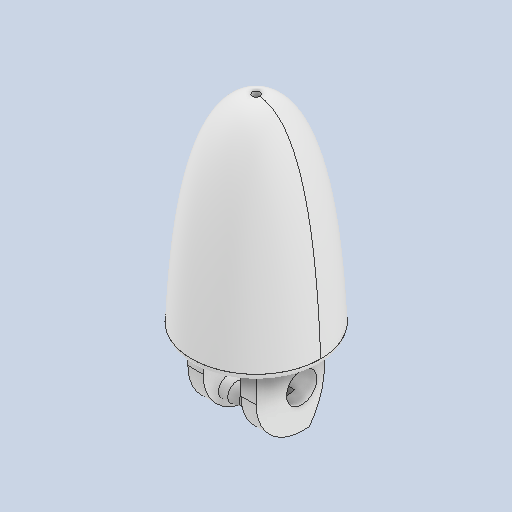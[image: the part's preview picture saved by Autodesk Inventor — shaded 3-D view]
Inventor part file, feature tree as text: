
AUTODESK INVENTOR PART (.ipt)
format: ipt  version: 2022 (Build 260153000, 153)  size: 346,624 bytes
history: native  units: in
note: dims shown in document units (in); Inventor stores cm internally (conversion verified against a paired STEP export)
features: sketch x6, fillet x5, extrude x4, hole x2, chamfer x2, plane x1, revolve x1
ambient origin geometry x8: Origin, YZ Plane, XZ Plane, XY Plane, X Axis, Y Axis, Z Axis, Center Point
bodies: Solid1 (feature_tree)
feature tree (21):
  extrude  "Extrusion1"  Depth=0.6693in
  extrude  "Extrusion2"  Depth=0.0394in TaperAngle=0.0deg
  fillet  "Fillet3"  Radius=0.0394in
  fillet  "Fillet4"  Radius=0.0394in
  fillet  "Fillet5"  Radius=0.2362in
  fillet  "Fillet6"  Radius=0.3937in
  hole  "Hole1"  [1 undecoded]
  extrude  "Extrusion3"  Depth=0.0984in TaperAngle=0.0deg
  chamfer  "Chamfer1"  Distance=0.0098in Angle=45.0deg
  extrude  "Extrusion4"  TaperAngle=360.0deg  [1 undecoded]
  chamfer  "Chamfer2"  Distance=0.1181in
  plane  "Work Plane1"
  revolve  "Revolution1"  [1 undecoded]
  hole  "Hole3"  [1 undecoded]
  fillet  "Fillet8"  [1 undecoded]
  sketch  "Sketch1"  dims[d8=0.3937in d9=0.0in d11=0.6693in]
  sketch  "Sketch2"  dims[d12=0.0984in d13=0.0394in d14=0.0in d18=0.0394in d19=0.0394in d22=0.2362in d23=0.3937in]
  sketch  "Sketch3"  dims[d24=0.1969in]
  sketch  "Sketch4"  dims[d25=0.1575in d26=0.2362in d27=0.1575in d28=0.0787in d29=90.0deg d30=0.3937in d31=0.0in d36=0.0984in d37=0.0in]
  sketch  "Sketch7"  dims[d38=0.0098in d39=0.0492in d40=45.0deg d41=0.0984in d42=0.0in d43=0.0098in d44=0.0492in d45=45.0deg]
  sketch  "Sketch9"  dims[d49=0.9449in d50=360.0deg d59=0.1181in d60=0.0394in d61=0.0394in d62=0.2362in d63=0.1575in d64=0.0787in d65=90.0deg d66=1.5748in d67=0.0in d68=0.0394in]
note: 5 required parameter values undecoded (feature->parameter linkage not recoverable at this tier; creation-order binding heuristic only, values carry confidence <= 0.55)